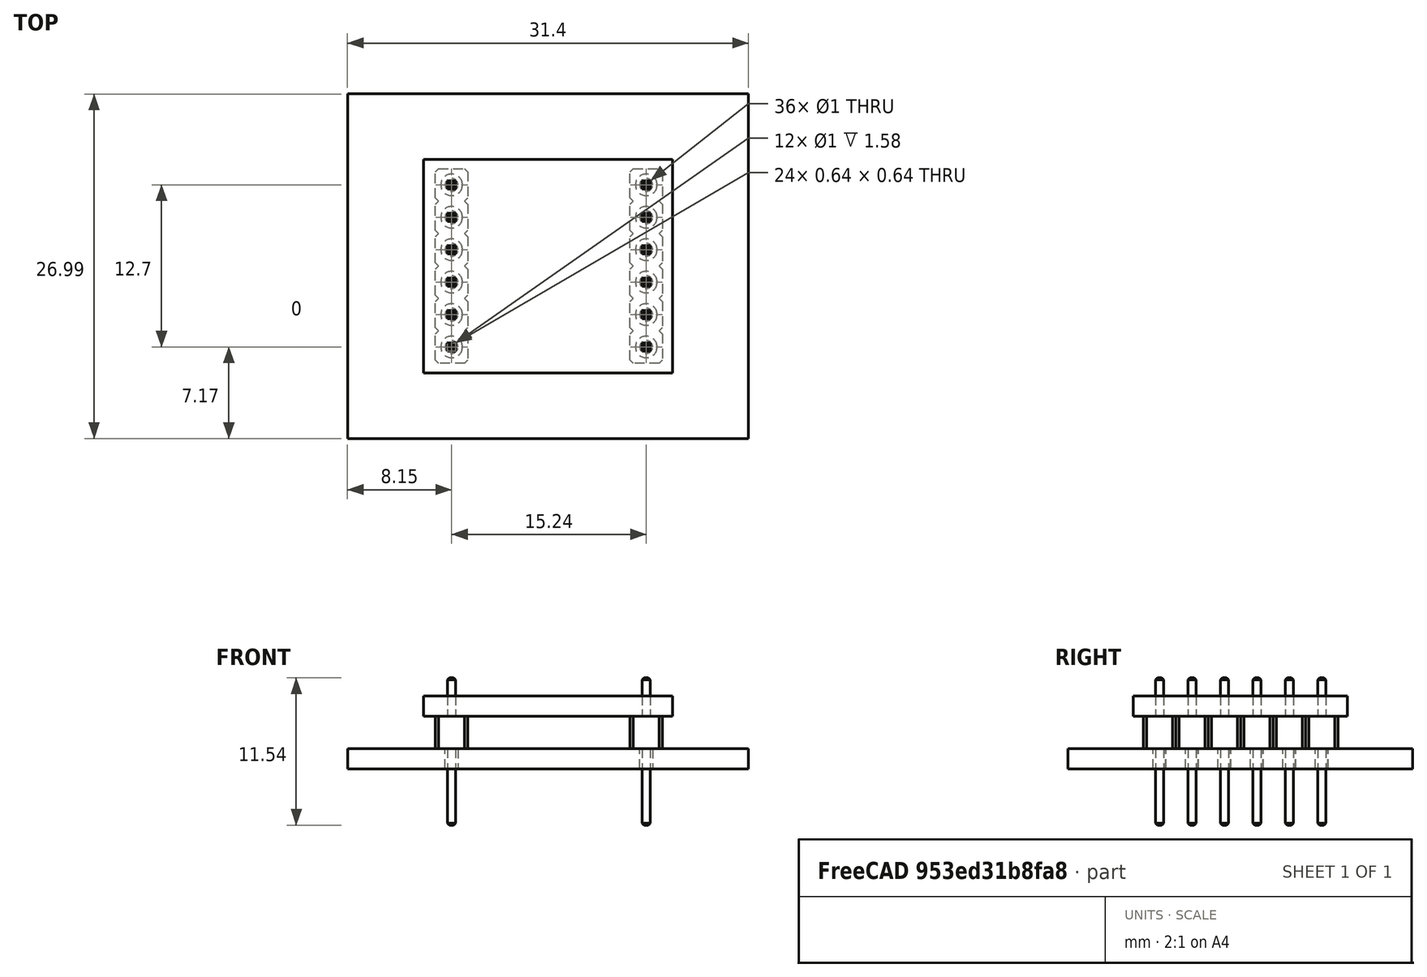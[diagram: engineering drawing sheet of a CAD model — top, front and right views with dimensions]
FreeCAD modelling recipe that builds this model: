
FCSTD DOCUMENT  (FreeCAD 0.19R)
Label: drv8833
License: All rights reserved
LicenseURL: http://en.wikipedia.org/wiki/All_rights_reserved
objects: Part::Feature×6, Part::FeaturePython×4, App::DocumentObjectGroup×1, PartDesign::ShapeBinder×1, PartDesign::Plane×1, Sketcher::SketchObject×1, PartDesign::Pad×1, Part::MultiFuse×1, Part::Compound×1
note: 17 computed .brp shape members not serialized (recipe doc carries the construction recipe); baked Part::Feature solids carry a one-line shape summary decoded from their .brp

FEATURE [Part::FeaturePython] FCrtYd_lines  label="FCrtYd"  # a2plus imported part (geometry in sourceFile) (typed FeaturePython)
  fixedPosition = true
FEATURE [Part::FeaturePython] FSilk_lines  label="FrontSilk"  # a2plus imported part (geometry in sourceFile) (typed FeaturePython)
  fixedPosition = true
FEATURE [Part::FeaturePython] THPs  label="PTHs"  # a2plus imported part (geometry in sourceFile) (typed FeaturePython)
  fixedPosition = true
FEATURE [Part::Feature] Shape001003  label="TopPads"
  shape: bbox 16.94 x 14.4 x 0.01 mm, 48 faces, 12 solids (baked)
FEATURE [Part::Feature] Shape001004  label="BotPads"
  shape: bbox 16.94 x 14.4 x 0.01 mm, 48 faces, 12 solids (baked)
FEATURE [Part::FeaturePython] newPCB  label="Pcb"  # a2plus imported part (geometry in sourceFile) (typed FeaturePython)
  fixedPosition = true
FEATURE [App::DocumentObjectGroup] drv8833_fp
  Group = -> [FCrtYd_lines,FSilk_lines,Shape001003,Shape001004,THPs,newPCB]
FEATURE [Part::Feature] Solid  label="PinHeader_1x06_P254mm_Vertical"
  Placement = pos=(0,-12.7,2.54) rot=(1,0,0;3.14159rad)
  shape: bbox 2.54 x 15.24 x 11.54 mm, 148 faces (baked)
FEATURE [Part::Feature] Solid001  label="PinHeader_1x06_P254mm_Vertical001"
  Placement = pos=(15.24,-12.7,2.54) rot=(1,0,0;3.14159rad)
  shape: bbox 2.54 x 15.24 x 11.54 mm, 148 faces (baked)
FEATURE [PartDesign::ShapeBinder] CopySolid
  Placement = pos=(0,-12.7,2.54) rot=(1,0,0;3.14159rad)
  TraceSupport = false
FEATURE [PartDesign::Plane] DatumPlane
  Length = 60
  MapMode = 5
  Placement = pos=(0,-12.7,2.54) rot=(0,0,1;0rad)
  ResizeMode = 0
  Support = -> [CopySolid]
  Width = 60
FEATURE [Sketcher::SketchObject] Sketch
  FullyConstrained = false
  MapMode = 5
  Placement = pos=(0,-12.7,2.54) rot=(0,0,1;0rad)
  Support = -> [DatumPlane]
  sketch-geometry (4):
    g0: LineSegment StartX=-2.19888 StartY=14.698 StartZ=0 EndX=17.3013 EndY=14.698 EndZ=0
    g1: LineSegment StartX=17.3013 StartY=14.698 StartZ=0 EndX=17.3013 EndY=-2.05016 EndZ=0
    g2: LineSegment StartX=17.3013 StartY=-2.05016 StartZ=0 EndX=-2.19888 EndY=-2.05016 EndZ=0
    g3: LineSegment StartX=-2.19888 StartY=-2.05016 StartZ=0 EndX=-2.19888 EndY=14.6979 EndZ=0
  constraints (8):
    c: Coincident(g0,g1)
    c: Coincident(g1,g2)
    c: Coincident(g2,g3)
    c: Coincident(g3,g0)
    c: Horizontal(g0)
    c: Horizontal(g2)
    c: Vertical(g1)
    c: Vertical(g3)
FEATURE [PartDesign::Pad] Pad
  Direction = (1,1,1)
  Length = 1.58
  Length2 = 100
  Placement = pos=(0,-12.7,2.54) rot=(0,0,1;0rad)
  Profile = -> Sketch
  Type = 0
FEATURE [Part::Feature] Shape  label="Body"
  shape: bbox 19.5 x 16.75 x 1.58 mm, 6 faces (baked)
FEATURE [Part::MultiFuse] Fusion
  Shapes = -> [Solid,Solid001]
FEATURE [Part::Compound] Compound
  Links = -> [Pad]
FEATURE [Part::Feature] Shape001006  label="Fusion001"
  shape: bbox 19.5 x 16.75 x 11.54 mm, 300 faces (baked)
